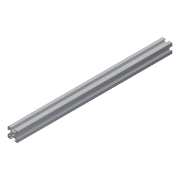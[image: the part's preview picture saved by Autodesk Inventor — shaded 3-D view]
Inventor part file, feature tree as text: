
AUTODESK INVENTOR PART (.ipt)
format: ipt  version: 2013 (Build 170138000, 138)  size: 279,552 bytes
history: native  units: in
note: dims shown in document units (in); Inventor stores cm internally (conversion verified against a paired STEP export)
features: other x3, extrude x1, sketch x1
ambient origin geometry x8: Origin, YZ Plane, XZ Plane, XY Plane, X Axis, Y Axis, Z Axis, Center Point
bodies: Solid1 (feature_tree)
feature tree (5):
  other  "Blocks"
  extrude  "Extrusion1"  [1 undecoded]
  sketch  "Sketch1"  dims[d1=0.0in]
  other  "20x20"
  other  "20x20:1"
note: 1 required parameter value undecoded (feature->parameter linkage not recoverable at this tier; creation-order binding heuristic only, values carry confidence <= 0.55)
